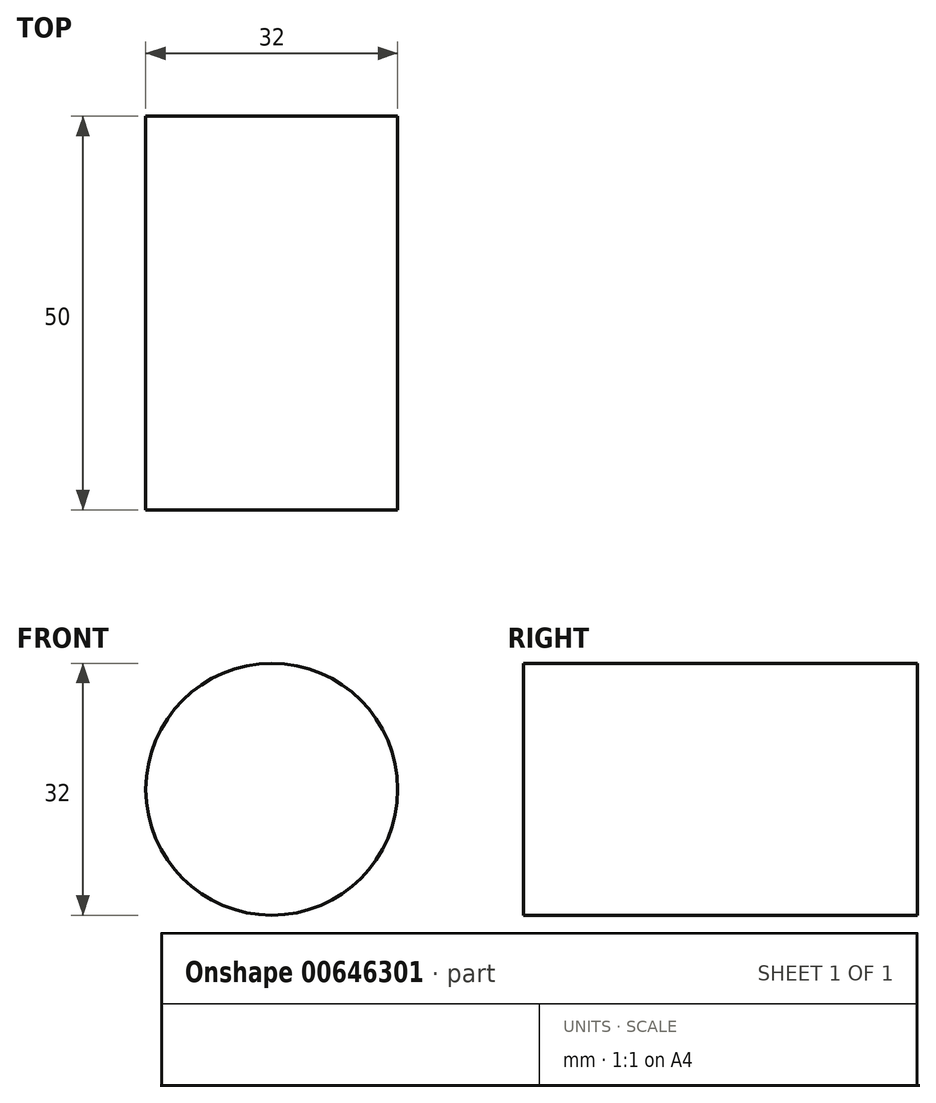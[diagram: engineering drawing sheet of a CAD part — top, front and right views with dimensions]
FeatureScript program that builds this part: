
annotation { "Feature Type Name" : "Feature", "Feature Type Description" : "" }
export const myFeature = defineFeature(function(context is Context, id is Id, definition is map)
    precondition{}
    {
        {
            var Q0;
            Q0=qCreatedBy(makeId("Front.planeOp"),FACE);
            var sketch = newSketch(context, id + "F0", { "sketchPlane" : qUnion([Q0])});
            skLineSegment(sketch, "E0", {"start": v(0, 0) * mm, "end": v(0, 32) * mm});
            skCircle(sketch, "E1", {"center": v(0, 16) * mm, "radius": 16 * mm});
            skSolve(sketch);
        }
        {
            var Q0;
            {var subQ0=sQuery(id+"F0.wireOp",EDGE,"E0");Q0=makeQuery(id+"F0.imprint","IMPRINT",FACE,{"disambiguationData":[TD([[makeQuery(id+"F0.imprint","IMPRINT",EDGE,{"derivedFrom":subQ0}),-1.0]])]});}
            var Q1;
            {var subQ0=sQuery(id+"F0.wireOp",EDGE,"E0");Q1=makeQuery(id+"F0.imprint","IMPRINT",FACE,{"disambiguationData":[TD([[makeQuery(id+"F0.imprint","IMPRINT",EDGE,{"derivedFrom":subQ0}),1.0]])]});}
            extrude(context, id + "F1", {"entities" : qUnion([Q0, Q1]), "depth" : 50 * mm, "offsetDistance" : 25 * mm});
        }
    });
